# Revit family: Omega Plate
name_source: partatom
category: Plumbing Fixtures
revit_build: Autodesk Revit 2017 (Build: 20160225_1515(x64)
units: mm (PartAtom-declared; Revit-internal decimal feet)

## family parameters
Cut with Voids When Loaded = No
Host = Face
Part Type = Normal
Room Calculation Point = No
Round Connector Dimension = Use Diameter
Shared = No

## types (15) — shared parameters
Default Elevation = 4' - 0"
Inlet Diameter = 0' - 0 1/2"
Manufacturer = Sioux Chief Manufacturing
Pipe Radius = 0' - 0 1/4"
URL = www.siouxchief.com

## per-type parameters (varying)
| type | 1807 Visibility | 1960 Visibility | CPVC Visibility | Connector Diameter | Description | MIP Visibility | Male Sweat in Visibility | Outlet Diameter |
| 699-A1-CR | No | No | Yes | 0' - 0 3/8" | Omegaplate | No | No | 0' - 0 9/16" |
| 699-A1-MR | No | No | No | 0' - 0 3/8" | Omegaplate | Yes | No | 0' - 0 9/16" |
| 699-A1-PR | No | No | No | 0' - 0 3/8" | Omegaplate | No | Yes | 0' - 0 9/16" |
| 699-A1-WR | No | Yes | No | 0' - 0 3/8" | Omegaplate | No | No | 0' - 0 9/16" |
| 699-A1-XR | Yes | No | No | 0' - 0 3/8" | Omegaplate | No | No | 0' - 0 9/16" |
| 699-A0-CR | No | No | Yes | 0' - 0 1/4" | Omegaplate | No | No | 0' - 0 7/16" |
| 699-A0-MR | No | No | No | 0' - 0 1/4" | Omegaplate | Yes | No | 0' - 0 7/16" |
| 699-A0-PR | No | No | No | 0' - 0 1/4" | Omegaplate | No | Yes | 0' - 0 7/16" |
| 699-A0-WR | No | Yes | No | 0' - 0 1/4" | Omegaplate | No | No | 0' - 0 7/16" |
| 699-A0-XR | Yes | No | No | 0' - 0 1/4" | Omgaplate | No | No | 0' - 0 7/16" |
| 699-A3-CR | No | No | Yes | 0' - 0 3/4" | Omegaplate | No | No | 0' - 0 29/32" |
| 699-A3-MR | No | No | No | 0' - 0 3/4" | Omegaplate | Yes | No | 0' - 0 29/32" |
| 699-A3-PR | No | No | No | 0' - 0 3/4" | Omegaplate | No | Yes | 0' - 0 29/32" |
| 699-A3-WR | No | Yes | No | 0' - 0 3/4" | Omegaplate | No | No | 0' - 0 29/32" |
| 699-A3-XR | Yes | No | No | 0' - 0 3/4" | Omegaplate | No | No | 0' - 0 29/32" |

note: column(s) folded — value = type name in every type: Model

## geometry (parser evidence)
native form markers: Sweep x14
no freeform markers — native parametric forms only
